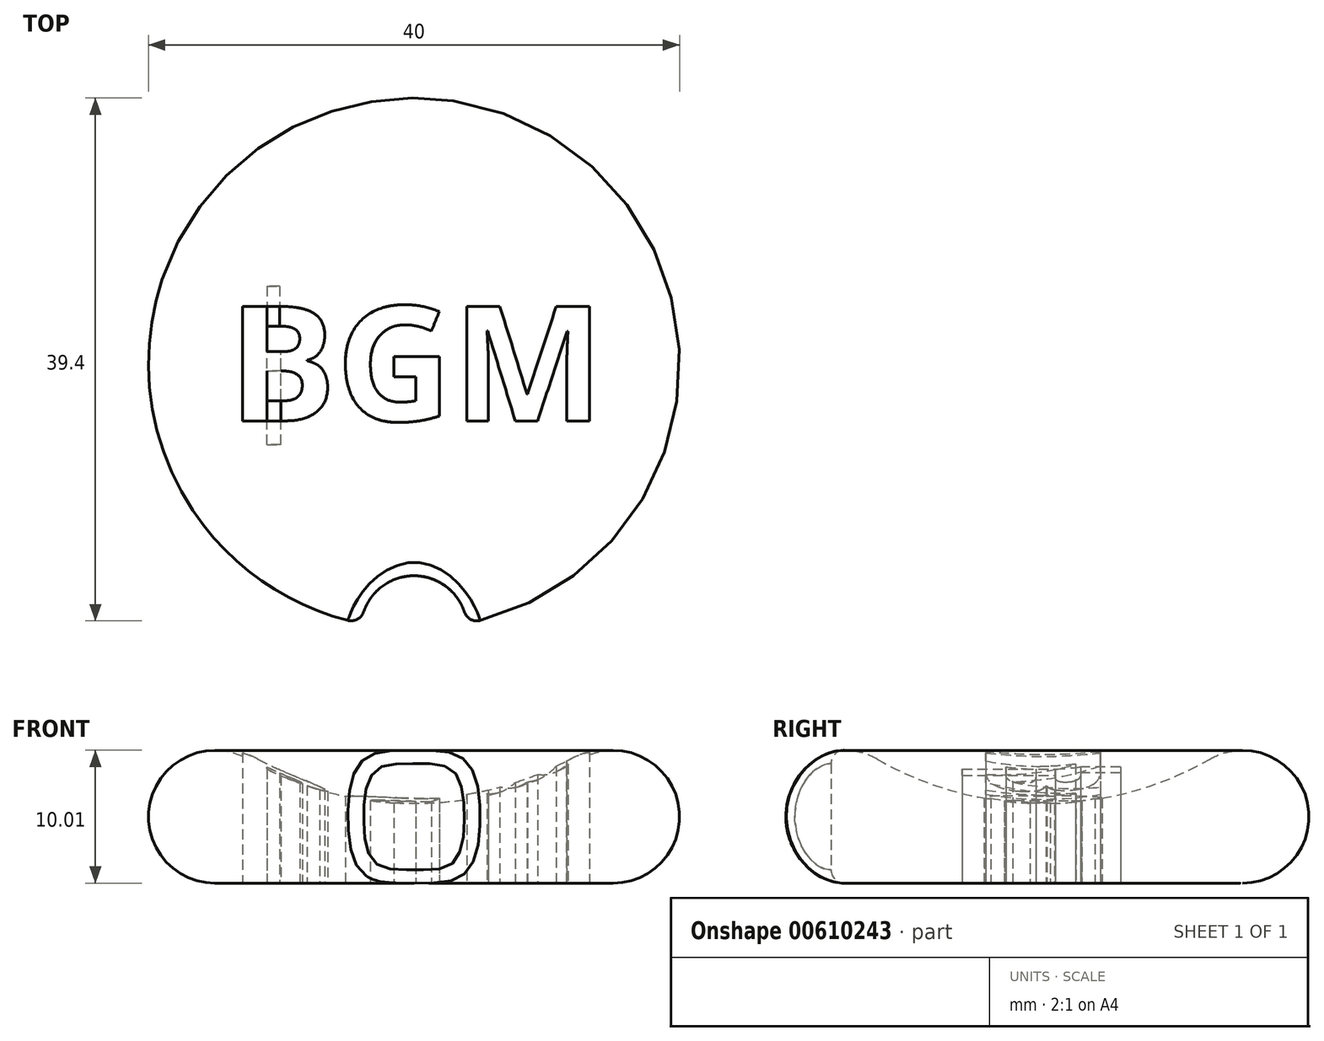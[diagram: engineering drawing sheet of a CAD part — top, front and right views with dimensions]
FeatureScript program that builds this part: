
annotation { "Feature Type Name" : "Feature", "Feature Type Description" : "" }
export const myFeature = defineFeature(function(context is Context, id is Id, definition is map)
    precondition{}
    {
        {
            var Q0;
            Q0=qCreatedBy(makeId("Front.planeOp"),FACE);
            var sketch = newSketch(context, id + "F0", { "sketchPlane" : qUnion([Q0])});
            skLineSegment(sketch, "E0", {"start": v(0, 0) * mm, "end": v(-15, 0) * mm});
            skLineSegment(sketch, "E1", {"start": v(0, 0) * mm, "end": v(0, 6) * mm});
            skPoint(sketch, "E2.center.orphan", {"position": v(0, 31.13) * mm});
            skArc(sketch, "E3", {"start": v(-12.51, 9.34) * mm, "mid": v(-19.83, 6.29) * mm, "end": v(-15, 0) * mm});
            skArc(sketch, "E4", {"start": v(-12.51, 9.34) * mm, "mid": v(-6.47, 6.85) * mm, "end": v(0, 6) * mm});
            skSolve(sketch);
        }
        {
            var Q0;
            Q0=makeQuery(id+"F0.imprint","IMPRINT",FACE,{"disambiguationData":[TD([[makeQuery(id+"F0.imprint","IMPRINT",EDGE,{"derivedFrom":sQuery(id+"F0.wireOp",EDGE,"E0")}),-1.0]])]});
            var Q1;
            Q1=sQuery(id+"F0.wireOp",EDGE,"E1");
            revolve(context, id + "F1", {"entities" : qUnion([Q0]), "axis" : qUnion([Q1]), "revolveType" : RevolveType.FULL});
        }
        {
            var Q0;
            Q0=qCreatedBy(makeId("Top.planeOp"),FACE);
            var sketch = newSketch(context, id + "F2", { "sketchPlane" : qUnion([Q0])});
            skText(sketch, "E5", { "text": "BGM", "fontName": "OpenSans-Bold.ttf"});
            const initialGuessF2  = {"E5": [-0.014, -0.00433, 1, 0, 0.00871]};
            skSetInitialGuess(sketch, initialGuessF2);
            skSolve(sketch);
        }
        {
            var Q0;
            Q0=makeQuery(id+"F2.imprint","IMPRINT",FACE,{"disambiguationData":[TD([[makeQuery(id+"F2.imprint","IMPRINT",EDGE,{"derivedFrom":sQuery(id+"F2.wireOp",EDGE,"E5.sketch_text.stroke-0")}),-1.0]])]});
            var Q1;
            Q1=makeQuery(id+"F2.imprint","IMPRINT",FACE,{"disambiguationData":[TD([[makeQuery(id+"F2.imprint","IMPRINT",EDGE,{"derivedFrom":sQuery(id+"F2.wireOp",EDGE,"E5.sketch_text.stroke-25")}),-1.0]])]});
            var Q2;
            Q2=makeQuery(id+"F2.imprint","IMPRINT",FACE,{"disambiguationData":[TD([[makeQuery(id+"F2.imprint","IMPRINT",EDGE,{"derivedFrom":sQuery(id+"F2.wireOp",EDGE,"E5.sketch_text.stroke-44")}),-1.0]])]});
            extrude(context, id + "F3", {"entities" : qUnion([Q0, Q1, Q2]), "operationType" : NewBodyOperationType.REMOVE, "depth" : 25 * mm, "offsetDistance" : 25 * mm});
        }
        {
            var Q0;
            Q0=qCreatedBy(makeId("Top.planeOp"),FACE);
            var sketch = newSketch(context, id + "F4", { "sketchPlane" : qUnion([Q0])});
            skCircle(sketch, "E6", {"center": v(0, -20) * mm, "radius": 4 * mm});
            skSolve(sketch);
        }
        {
            var Q0;
            Q0=makeQuery(id+"F4.imprint","IMPRINT",FACE,{"disambiguationData":[TD([[makeQuery(id+"F4.imprint","IMPRINT",EDGE,{"derivedFrom":sQuery(id+"F4.wireOp",EDGE,"E6")}),1.0]])]});
            extrude(context, id + "F5", {"entities" : qUnion([Q0]), "operationType" : NewBodyOperationType.REMOVE, "depth" : 25 * mm, "offsetDistance" : 25 * mm});
        }
        {
            var Q0;
            Q0 = qSketchRegion(id + "F4", true);
            var Q1;
            Q1=makeQuery(id+"F4.imprint","IMPRINT",FACE,{"disambiguationData":[TD([[makeQuery(id+"F4.imprint","IMPRINT",EDGE,{"derivedFrom":sQuery(id+"F4.wireOp",EDGE,"E6")}),1.0]])]});
            extrude(context, id + "F6", {"entities" : qUnion([Q0, Q1]), "operationType" : NewBodyOperationType.REMOVE, "depth" : 25 * mm, "offsetDistance" : 25 * mm});
        }
        {
            var Q0;
            Q0=makeQuery(id+"F6.boolean.opBoolean","INTERSECT",EDGE,{"derivedFrom":[makeQuery(id+"F3.boolean.opBoolean","SPLIT",FACE,{"disambiguationData":[TD([makeQuery(id+"F1.opRevolve","SWEPT_FACE",FACE,{"disambiguationData":[OSD([sQuery(id+"F0.wireOp",EDGE,"E0")])]})])],"derivedFrom":makeQuery(id+"F1.opRevolve","SWEPT_FACE",FACE,{"disambiguationData":[OSD([sQuery(id+"F0.wireOp",EDGE,"E3")])]})}),makeQuery(id+"F6.opExtrude","SWEPT_FACE",FACE,{"disambiguationData":[OSD([sQuery(id+"F4.wireOp",EDGE,"E6")])]})]});
            var Q1;
            Q1=makeQuery(id+"F5.boolean.opBoolean","INTERSECT",EDGE,{"derivedFrom":[makeQuery(id+"F1.opRevolve","SWEPT_FACE",FACE,{"disambiguationData":[OSD([sQuery(id+"F0.wireOp",EDGE,"E3")])]}),makeQuery(id+"F5.opExtrude","SWEPT_FACE",FACE,{"disambiguationData":[OSD([sQuery(id+"F4.wireOp",EDGE,"E6")])]})]});
            fillet(context, id + "F7", {"entities" : qUnion([Q0, Q1]), "radius" : 1 * mm, "tangentPropagation" : true, "allowEdgeOverflow" : false});
        }
        {
            var Q0;
            Q0=makeQuery(id+"F3.boolean.opBoolean","COPY",FACE,{"derivedFrom":makeQuery(id+"F3.opExtrude","SWEPT_FACE",FACE,{"disambiguationData":[OSD([sQuery(id+"F2.wireOp",EDGE,"E5.sketch_text.stroke-17")])]})});
            extrude(context, id + "F8", {"entities" : qUnion([Q0]), "depth" : 3 * mm, "offsetDistance" : 25 * mm});
        }
        {
            var Q0;
            Q0=makeQuery(id+"F3.boolean.opBoolean","COPY",FACE,{"derivedFrom":makeQuery(id+"F3.opExtrude","SWEPT_FACE",FACE,{"disambiguationData":[OSD([sQuery(id+"F2.wireOp",EDGE,"E5.sketch_text.stroke-12")])]})});
            extrude(context, id + "F9", {"entities" : qUnion([Q0]), "depth" : 7 * mm, "offsetDistance" : 25 * mm});
        }
        {
            var Q0;
            Q0 = qSketchRegion(id + "F4", true);
            var Q1;
            Q1=makeQuery(id+"F4.imprint","IMPRINT",FACE,{"disambiguationData":[TD([[makeQuery(id+"F4.imprint","IMPRINT",EDGE,{"derivedFrom":sQuery(id+"F4.wireOp",EDGE,"E6")}),1.0]])]});
            extrude(context, id + "F10", {"entities" : qUnion([Q0, Q1]), "operationType" : NewBodyOperationType.REMOVE, "oppositeDirection" : true, "depth" : 25 * mm, "offsetDistance" : 25 * mm});
        }
    });
